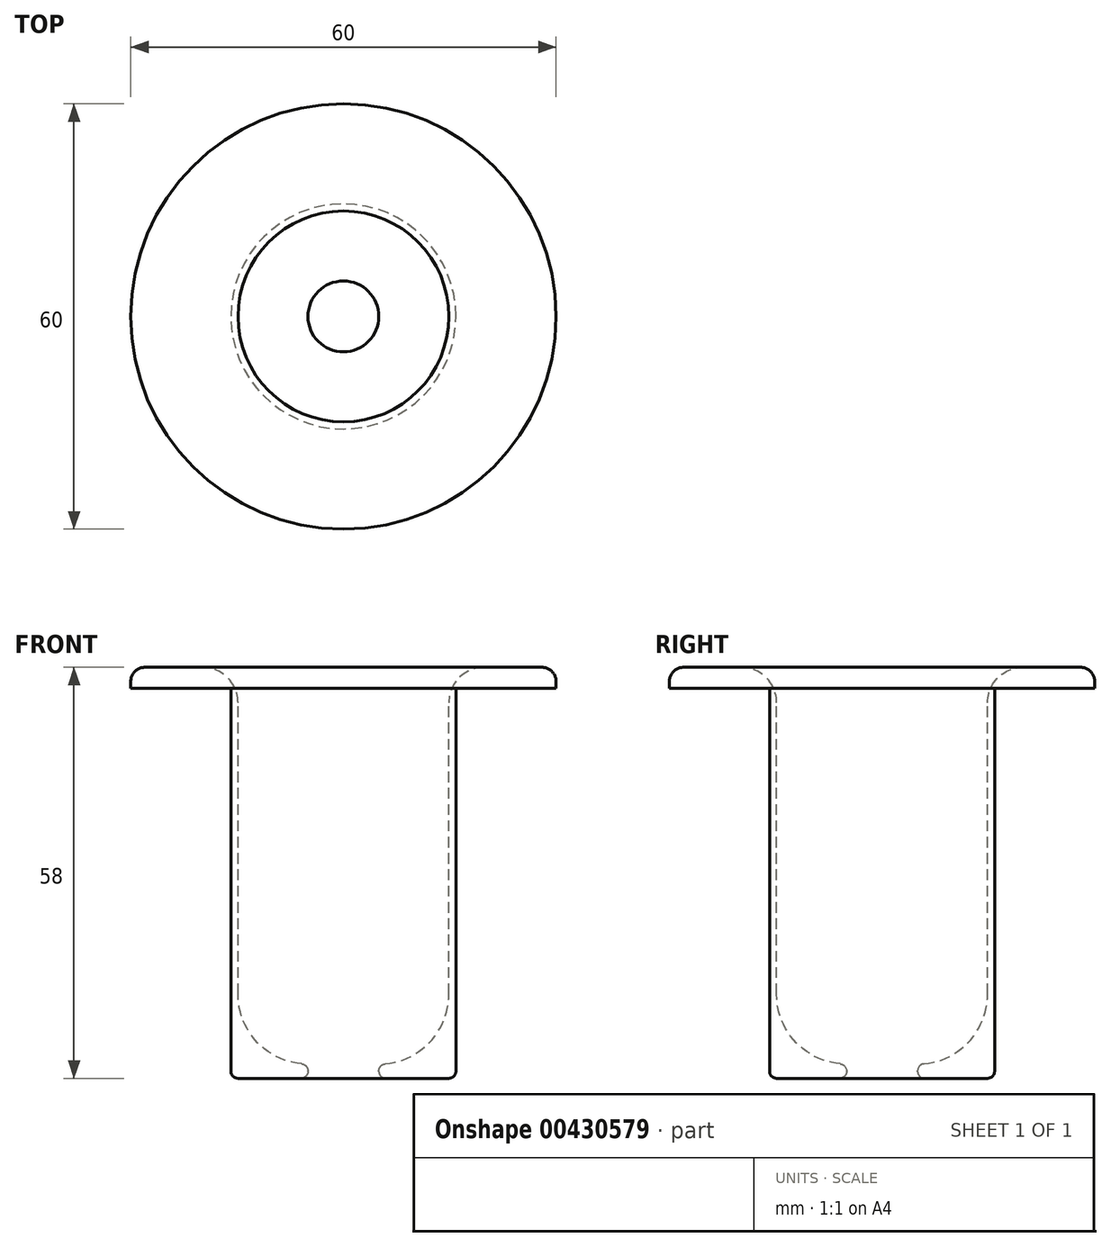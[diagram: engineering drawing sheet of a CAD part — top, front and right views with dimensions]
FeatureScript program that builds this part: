
annotation { "Feature Type Name" : "Feature", "Feature Type Description" : "" }
export const myFeature = defineFeature(function(context is Context, id is Id, definition is map)
    precondition{}
    {
        {
            var Q0;
            Q0=qCreatedBy(makeId("Front.planeOp"),FACE);
            var sketch = newSketch(context, id + "F0", { "sketchPlane" : qUnion([Q0])});
            skLineSegment(sketch, "E0.bottom", {"start": v(-14.88, 37.03) * mm, "end": v(-15.88, 37.03) * mm});
            skLineSegment(sketch, "E0.top", {"start": v(-14.88, -20.97) * mm, "end": v(-15.88, -20.97) * mm});
            skLineSegment(sketch, "E0.left", {"start": v(-14.88, 37.03) * mm, "end": v(-14.87, -20.97) * mm});
            skLineSegment(sketch, "E0.right", {"start": v(-15.88, 37.03) * mm, "end": v(-15.87, -20.97) * mm});
            skLineSegment(sketch, "E1.bottom", {"start": v(-14.88, 37.03) * mm, "end": v(-30, 37.03) * mm});
            skLineSegment(sketch, "E1.top", {"start": v(-14.88, 34.03) * mm, "end": v(-30, 34.03) * mm});
            skLineSegment(sketch, "E1.left", {"start": v(-14.88, 37.03) * mm, "end": v(-14.88, 34.03) * mm});
            skLineSegment(sketch, "E1.right", {"start": v(-30, 37.03) * mm, "end": v(-30, 34.03) * mm});
            skLineSegment(sketch, "E2.bottom", {"start": v(-14.88, -20.97) * mm, "end": v(-5, -20.97) * mm});
            skLineSegment(sketch, "E2.top", {"start": v(-14.88, -18.97) * mm, "end": v(-5, -18.97) * mm});
            skLineSegment(sketch, "E2.left", {"start": v(-14.87, -20.97) * mm, "end": v(-14.87, -18.97) * mm});
            skLineSegment(sketch, "E2.right", {"start": v(-5, -20.97) * mm, "end": v(-5, -18.97) * mm});
            skArc(sketch, "E3", {"start": v(-14.87, -9.1) * mm, "mid": v(-11.98, -16.08) * mm, "end": v(-5, -18.97) * mm});
            skLineSegment(sketch, "E4", {"start": v(0, 15.9) * mm, "end": v(0, -8.81) * mm});
            skSolve(sketch);
        }
        {
            var Q0;
            {var subQ1=sQuery(id+"F0.wireOp",EDGE,"E0.top");Q0=makeQuery(id+"F0.imprint","IMPRINT",FACE,{"disambiguationData":[TD([[makeQuery(id+"F0.imprint","IMPRINT",EDGE,{"derivedFrom":subQ1}),-1.0]])]});}
            var Q1;
            {var subQ0=sQuery(id+"F0.wireOp",EDGE,"E1.bottom");Q1=makeQuery(id+"F0.imprint","IMPRINT",FACE,{"disambiguationData":[TD([[makeQuery(id+"F0.imprint","IMPRINT",EDGE,{"derivedFrom":subQ0}),1.0]])]});}
            var Q2;
            {var subQ0=sQuery(id+"F0.wireOp",EDGE,"E2.bottom");Q2=makeQuery(id+"F0.imprint","IMPRINT",FACE,{"disambiguationData":[TD([[makeQuery(id+"F0.imprint","IMPRINT",EDGE,{"derivedFrom":subQ0}),1.0]])]});}
            var Q3;
            {var subQ0=sQuery(id+"F0.wireOp",EDGE,"E0.bottom");Q3=makeQuery(id+"F0.imprint","IMPRINT",FACE,{"disambiguationData":[TD([[makeQuery(id+"F0.imprint","IMPRINT",EDGE,{"derivedFrom":subQ0}),1.0]])]});}
            var Q4;
            {var subQ0=sQuery(id+"F0.wireOp",EDGE,"E2.top");Q4=makeQuery(id+"F0.imprint","IMPRINT",FACE,{"disambiguationData":[TD([[makeQuery(id+"F0.imprint","IMPRINT",EDGE,{"derivedFrom":subQ0}),1.0]])]});}
            var Q5;
            Q5=sQuery(id+"F0.wireOp",EDGE,"E4");
            revolve(context, id + "F1", {"surfaceOperationType" : NewSurfaceOperationType.NEW, "entities" : qUnion([Q0, Q1, Q2, Q3, Q4]), "axis" : qUnion([Q5]), "revolveType" : RevolveType.FULL});
        }
        {
            var Q0;
            Q0=makeQuery(id+"F1.opRevolve","SWEPT_EDGE",EDGE,{"disambiguationData":[OSD([sQuery(id+"F0.wireOp",EDGE,"E2.bottom"),sQuery(id+"F0.wireOp",EDGE,"E2.right")])]});
            var Q1;
            Q1=makeQuery(id+"F1.opRevolve","SWEPT_EDGE",EDGE,{"disambiguationData":[OSD([sQuery(id+"F0.wireOp",EDGE,"E2.top"),sQuery(id+"F0.wireOp",EDGE,"E2.right"),sQuery(id+"F0.wireOp",EDGE,"E3")])]});
            var Q2;
            Q2=makeQuery(id+"F1.opRevolve","SWEPT_FACE",FACE,{"disambiguationData":[OSD([sQuery(id+"F0.wireOp",EDGE,"E0.top"),sQuery(id+"F0.wireOp",EDGE,"E2.bottom")])]});
            fillet(context, id + "F2", {"entities" : qUnion([Q0, Q1, Q2]), "tangentPropagation" : true, "radius" : 1 * mm, "defaultsChanged" : false, "vertexSettings" : [], "allowEdgeOverflow" : false});
        }
        {
            var Q0;
            Q0=makeQuery(id+"F1.opRevolve","SWEPT_EDGE",EDGE,{"disambiguationData":[OSD([sQuery(id+"F0.wireOp",EDGE,"E0.bottom"),sQuery(id+"F0.wireOp",EDGE,"E0.left")])]});
            fillet(context, id + "F3", {"entities" : qUnion([Q0]), "tangentPropagation" : true, "radius" : 5 * mm, "defaultsChanged" : false, "vertexSettings" : [], "allowEdgeOverflow" : false});
        }
        {
            var Q0;
            Q0=makeQuery(id+"F1.opRevolve","SWEPT_EDGE",EDGE,{"disambiguationData":[OSD([sQuery(id+"F0.wireOp",EDGE,"E1.bottom"),sQuery(id+"F0.wireOp",EDGE,"E1.right")])]});
            fillet(context, id + "F4", {"entities" : qUnion([Q0]), "tangentPropagation" : true, "radius" : 2 * mm, "defaultsChanged" : true, "vertexSettings" : [], "allowEdgeOverflow" : false});
        }
    });
